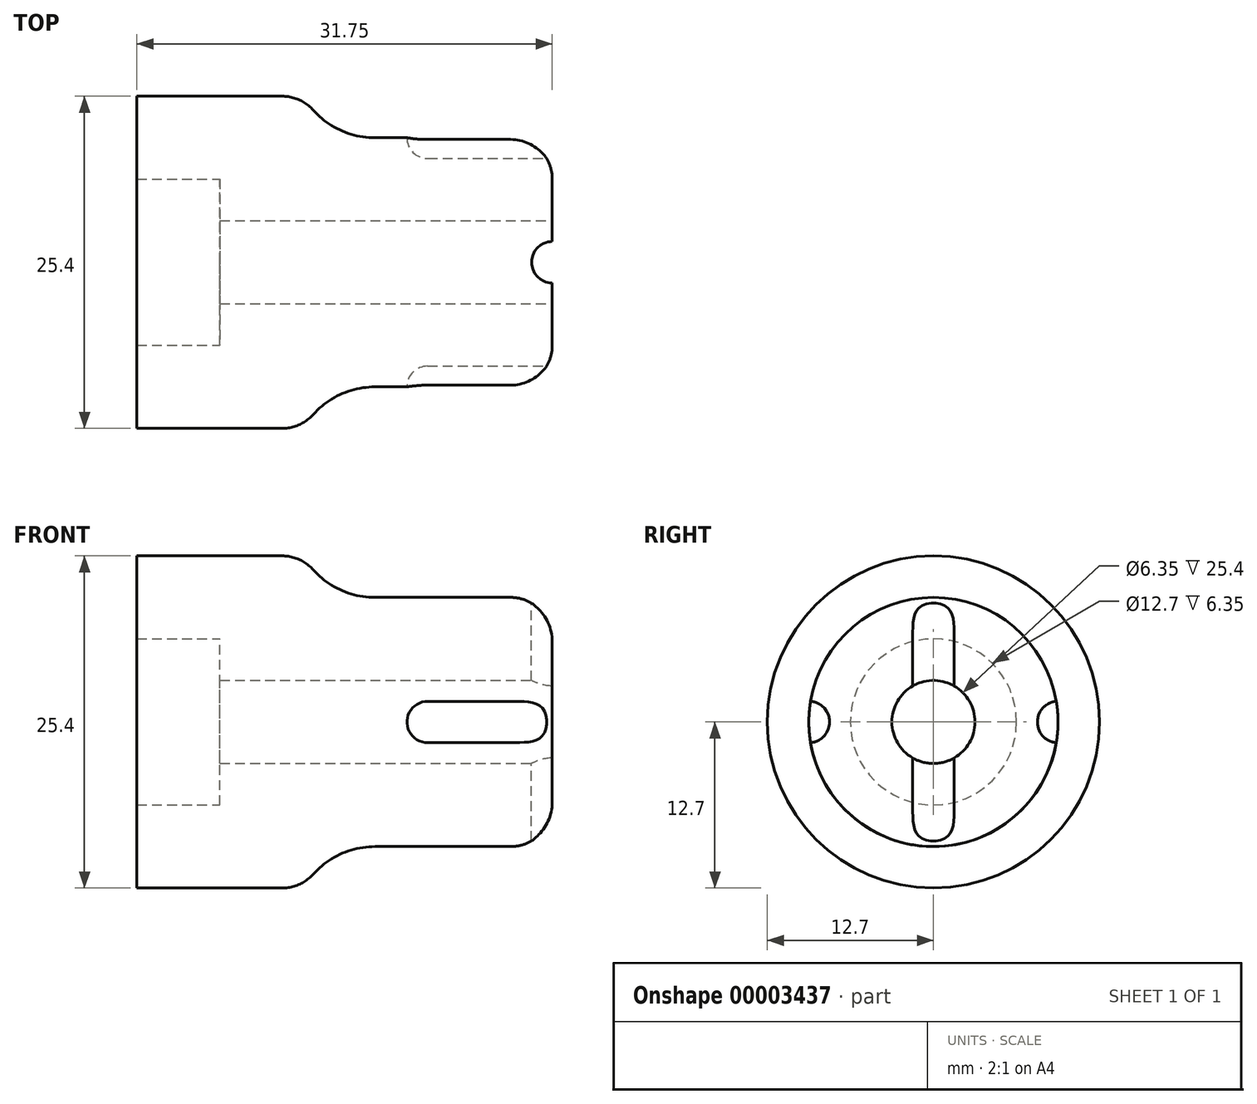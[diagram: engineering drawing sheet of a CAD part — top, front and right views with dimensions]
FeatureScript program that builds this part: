
annotation { "Feature Type Name" : "Feature", "Feature Type Description" : "" }
export const myFeature = defineFeature(function(context is Context, id is Id, definition is map)
    precondition{}
    {
        {
            var Q0;
            Q0=qCreatedBy(makeId("Front.planeOp"),FACE);
            var sketch = newSketch(context, id + "F0", { "sketchPlane" : qUnion([Q0])});
            skLineSegment(sketch, "E0", {"start": v(0, 3.18) * mm, "end": v(0, 9.53) * mm});
            skLineSegment(sketch, "E1", {"start": v(0, 9.53) * mm, "end": v(-19.05, 9.53) * mm});
            skLineSegment(sketch, "E2", {"start": v(-19.05, 9.53) * mm, "end": v(-19.05, 12.7) * mm});
            skLineSegment(sketch, "E3", {"start": v(-19.05, 12.7) * mm, "end": v(-31.75, 12.7) * mm});
            skLineSegment(sketch, "E4", {"start": v(-31.75, 12.7) * mm, "end": v(-31.75, 6.35) * mm});
            skLineSegment(sketch, "E5", {"start": v(-31.75, 6.35) * mm, "end": v(-25.4, 6.35) * mm});
            skLineSegment(sketch, "E6", {"start": v(-25.4, 6.35) * mm, "end": v(-25.4, 3.18) * mm});
            skLineSegment(sketch, "E7", {"start": v(-25.4, 3.18) * mm, "end": v(0, 3.18) * mm});
            skLineSegment(sketch, "E8", {"start": v(0, 0) * mm, "end": v(-59.15, 0) * mm, "construction": true});
            skSolve(sketch);
        }
        {
            var Q0;
            Q0=makeQuery(id+"F0.imprint","IMPRINT",FACE,{"disambiguationData":[TD([[makeQuery(id+"F0.imprint","IMPRINT",EDGE,{"derivedFrom":sQuery(id+"F0.wireOp",EDGE,"E0")}),1.0]])]});
            var Q1;
            Q1=sQuery(id+"F0.wireOp",EDGE,"E8");
            revolve(context, id + "F1", {"entities" : qUnion([Q0]), "axis" : qUnion([Q1]), "revolveType" : RevolveType.FULL});
        }
        {
            var Q0;
            Q0=makeQuery(id+"F1.opRevolve","SWEPT_EDGE",EDGE,{"disambiguationData":[OSD([sQuery(id+"F0.wireOp",EDGE,"E1"),sQuery(id+"F0.wireOp",EDGE,"E2")])]});
            fillet(context, id + "F2", {"entities" : qUnion([Q0]), "radius" : 6.35 * mm, "tangentPropagation" : true, "allowEdgeOverflow" : false});
        }
        {
            var Q0;
            Q0=makeQuery(id+"F1.opRevolve","SWEPT_EDGE",EDGE,{"disambiguationData":[OSD([sQuery(id+"F0.wireOp",EDGE,"E0"),sQuery(id+"F0.wireOp",EDGE,"E1")])]});
            var Q1;
            Q1=makeQuery(id+"F2.opFillet","BLEND_EDGE",EDGE,{"blendedFrom":[makeQuery(id+"F1.opRevolve","SWEPT_EDGE",EDGE,{"disambiguationData":[OSD([sQuery(id+"F0.wireOp",EDGE,"E1"),sQuery(id+"F0.wireOp",EDGE,"E2")])]}),makeQuery(id+"F1.opRevolve","SWEPT_FACE",FACE,{"disambiguationData":[OSD([sQuery(id+"F0.wireOp",EDGE,"E3")])]})],"blendedInto":[makeQuery(id+"F1.opRevolve","SWEPT_FACE",FACE,{"disambiguationData":[OSD([sQuery(id+"F0.wireOp",EDGE,"E3")])]})]});
            fillet(context, id + "F3", {"entities" : qUnion([Q0, Q1]), "radius" : 3.17 * mm, "tangentPropagation" : true, "allowEdgeOverflow" : false});
        }
        {
            var Q0;
            Q0=qCreatedBy(makeId("Top.planeOp"),FACE);
            var sketch = newSketch(context, id + "F4", { "sketchPlane" : qUnion([Q0])});
            skCircle(sketch, "E9", {"center": v(0, 0) * mm, "radius": 1.59 * mm});
            skSolve(sketch);
        }
        {
            var Q0;
            Q0=makeQuery(id+"F4.imprint","IMPRINT",FACE,{"disambiguationData":[TD([[makeQuery(id+"F4.imprint","IMPRINT",EDGE,{"derivedFrom":sQuery(id+"F4.wireOp",EDGE,"E9")}),1.0]])]});
            extrude(context, id + "F5", {"entities" : qUnion([Q0]), "operationType" : NewBodyOperationType.REMOVE, "oppositeDirection" : true, "depth" : 25.4 * mm, "symmetric" : true});
        }
        {
            var Q0;
            Q0=makeQuery(id+"F5.boolean.opBoolean","SPLIT",FACE,{"disambiguationData":[OD(1.0)],"derivedFrom":makeQuery(id+"F1.opRevolve","SWEPT_FACE",FACE,{"disambiguationData":[OSD([sQuery(id+"F0.wireOp",EDGE,"E0")])]})});
            var sketch = newSketch(context, id + "F6", { "sketchPlane" : qUnion([Q0])});
            skCircle(sketch, "E10", {"center": v(9.53, 0) * mm, "radius": 1.59 * mm});
            skLineSegment(sketch, "E11", {"start": v(9.53, 0) * mm, "end": v(0, 0) * mm, "construction": true});
            skCircle(sketch, "E12", {"center": v(-9.53, 0) * mm, "radius": 1.59 * mm});
            skSolve(sketch);
        }
        {
            var Q0;
            {var subQ0=sQuery(id+"F0.wireOp",EDGE,"E0");var subQ1=makeQuery(id+"F5.boolean.opBoolean","SPLIT",EDGE,{"disambiguationData":[OD(1.0)],"derivedFrom":makeQuery(id+"F3.opFillet","BLEND_EDGE",EDGE,{"blendedFrom":[makeQuery(id+"F1.opRevolve","SWEPT_EDGE",EDGE,{"disambiguationData":[OSD([subQ0,sQuery(id+"F0.wireOp",EDGE,"E1")])]}),makeQuery(id+"F1.opRevolve","SWEPT_FACE",FACE,{"disambiguationData":[OSD([subQ0])]})],"blendedInto":[makeQuery(id+"F1.opRevolve","SWEPT_FACE",FACE,{"disambiguationData":[OSD([subQ0])]})]})});var subQ2=sQuery(id+"F6.wireOp",EDGE,"E10");var subQ4=makeQuery(id+"F6.imprint","INTERSECT",VERTEX,{"disambiguationData":[OD(0.0)],"derivedFrom":[subQ1,subQ2]});Q0=qUnion([makeQuery(id+"F6.imprint","IMPRINT",FACE,{"disambiguationData":[TD([[makeQuery(id+"F6.imprint","IMPRINT",EDGE,{"derivedFrom":sQuery(id+"F6.wireOp",EDGE,"E12")}),1.0]])]}),makeQuery(id+"F6.imprint","IMPRINT",FACE,{"disambiguationData":[TD([[makeQuery(id+"F6.imprint","IMPRINT",EDGE,{"disambiguationData":[TD([[subQ4,-1.0]])],"derivedFrom":subQ2}),1.0]])]}),makeQuery(id+"F6.imprint","IMPRINT",FACE,{"disambiguationData":[TD([[makeQuery(id+"F6.imprint","IMPRINT",EDGE,{"disambiguationData":[TD([[subQ4,1.0]])],"derivedFrom":subQ2}),1.0]])]})]);}
            extrude(context, id + "F7", {"entities" : qUnion([Q0]), "operationType" : NewBodyOperationType.REMOVE, "oppositeDirection" : true, "depth" : 9.52 * mm});
        }
        {
            var Q0;
            Q0=makeQuery(id+"F7.boolean.opBoolean","COPY",FACE,{"derivedFrom":makeQuery(id+"F7.opExtrude","CAP_FACE",FACE,{"disambiguationData":[OSD([sQuery(id+"F6.wireOp",EDGE,"E12")])],"isStart":false})});
            var sketch = newSketch(context, id + "F8", { "sketchPlane" : qUnion([Q0])});
            skLineSegment(sketch, "E13", {"start": v(-9.53, 1.59) * mm, "end": v(-9.53, -1.59) * mm});
            skArc(sketch, "E14.converted", {"start": v(-9.53, -1.59) * mm, "mid": v(-7.94, 0) * mm, "end": v(-9.53, 1.59) * mm});
            skPoint(sketch, "E15.orphan", {"position": v(-9.4, 1.58) * mm});
            skSolve(sketch);
        }
        {
            var Q0;
            {var subQ0=makeQuery(id+"F7.boolean.opBoolean","INTERSECT",EDGE,{"derivedFrom":[makeQuery(id+"F1.opRevolve","SWEPT_FACE",FACE,{"disambiguationData":[OSD([sQuery(id+"F0.wireOp",EDGE,"E1")])]}),makeQuery(id+"F7.opExtrude","CAP_FACE",FACE,{"disambiguationData":[OSD([sQuery(id+"F6.wireOp",EDGE,"E12")])],"isStart":false})]});var subQ1=sQuery(id+"F8.wireOp",EDGE,"E13");var subQ3=sQuery(id+"F8.wireOp",EDGE,"E14.converted");var subQ6=makeQuery(id+"F8.imprint","INTERSECT",VERTEX,{"disambiguationData":[OD(0.0)],"derivedFrom":[subQ1,subQ3]});var subQ7=makeQuery(id+"F8.imprint","INTERSECT",VERTEX,{"disambiguationData":[OD(0.0)],"derivedFrom":[subQ0,subQ3]});var subQ9=makeQuery(id+"F8.imprint","INTERSECT",VERTEX,{"disambiguationData":[OD(1.0)],"derivedFrom":[subQ1,subQ3]});Q0=qUnion([makeQuery(id+"F8.imprint","IMPRINT",FACE,{"disambiguationData":[TD([[makeQuery(id+"F8.imprint","IMPRINT",EDGE,{"disambiguationData":[TD([[subQ6,-1.0]])],"derivedFrom":subQ1}),1.0]])]}),makeQuery(id+"F8.imprint","IMPRINT",FACE,{"disambiguationData":[TD([[makeQuery(id+"F8.imprint","IMPRINT",EDGE,{"disambiguationData":[TD([[subQ9,1.0]])],"derivedFrom":subQ1}),1.0]])]}),makeQuery(id+"F8.imprint","IMPRINT",FACE,{"disambiguationData":[TD([[makeQuery(id+"F8.imprint","IMPRINT",EDGE,{"disambiguationData":[TD([[subQ7,-1.0]])],"derivedFrom":subQ3}),1.0]])]})]);}
            var Q1;
            Q1=sQuery(id+"F8.wireOp",EDGE,"E13");
            revolve(context, id + "F9", {"operationType" : NewBodyOperationType.REMOVE, "entities" : qUnion([Q0]), "axis" : qUnion([Q1]), "revolveType" : RevolveType.FULL, "oppositeDirection" : true});
        }
        {
            var Q0;
            Q0=makeQuery(id+"F7.boolean.opBoolean","COPY",FACE,{"derivedFrom":makeQuery(id+"F7.opExtrude","CAP_FACE",FACE,{"disambiguationData":[OSD([sQuery(id+"F6.wireOp",EDGE,"E10")])],"isStart":false})});
            var sketch = newSketch(context, id + "F10", { "sketchPlane" : qUnion([Q0])});
            skLineSegment(sketch, "E16", {"start": v(9.53, 1.59) * mm, "end": v(9.53, -1.59) * mm});
            skArc(sketch, "E17.converted", {"start": v(9.53, 1.59) * mm, "mid": v(7.94, 0) * mm, "end": v(9.53, -1.59) * mm});
            skPoint(sketch, "E18.orphan", {"position": v(9.4, 1.58) * mm});
            skSolve(sketch);
        }
        {
            var Q0;
            {var subQ0=makeQuery(id+"F7.boolean.opBoolean","INTERSECT",EDGE,{"derivedFrom":[makeQuery(id+"F1.opRevolve","SWEPT_FACE",FACE,{"disambiguationData":[OSD([sQuery(id+"F0.wireOp",EDGE,"E1")])]}),makeQuery(id+"F7.opExtrude","CAP_FACE",FACE,{"disambiguationData":[OSD([sQuery(id+"F6.wireOp",EDGE,"E10")])],"isStart":false})]});var subQ1=sQuery(id+"F10.wireOp",EDGE,"E16");var subQ3=sQuery(id+"F10.wireOp",EDGE,"E17.converted");var subQ6=makeQuery(id+"F10.imprint","INTERSECT",VERTEX,{"disambiguationData":[OD(0.0)],"derivedFrom":[subQ1,subQ3]});var subQ7=makeQuery(id+"F10.imprint","INTERSECT",VERTEX,{"disambiguationData":[OD(0.0)],"derivedFrom":[subQ0,subQ3]});var subQ9=makeQuery(id+"F10.imprint","INTERSECT",VERTEX,{"disambiguationData":[OD(1.0)],"derivedFrom":[subQ1,subQ3]});Q0=qUnion([makeQuery(id+"F10.imprint","IMPRINT",FACE,{"disambiguationData":[TD([[makeQuery(id+"F10.imprint","IMPRINT",EDGE,{"disambiguationData":[TD([[subQ6,-1.0]])],"derivedFrom":subQ1}),-1.0]])]}),makeQuery(id+"F10.imprint","IMPRINT",FACE,{"disambiguationData":[TD([[makeQuery(id+"F10.imprint","IMPRINT",EDGE,{"disambiguationData":[TD([[subQ9,1.0]])],"derivedFrom":subQ1}),-1.0]])]}),makeQuery(id+"F10.imprint","IMPRINT",FACE,{"disambiguationData":[TD([[makeQuery(id+"F10.imprint","IMPRINT",EDGE,{"disambiguationData":[TD([[subQ7,1.0]])],"derivedFrom":subQ3}),1.0]])]})]);}
            var Q1;
            Q1=sQuery(id+"F10.wireOp",EDGE,"E16");
            revolve(context, id + "F11", {"operationType" : NewBodyOperationType.REMOVE, "entities" : qUnion([Q0]), "axis" : qUnion([Q1]), "revolveType" : RevolveType.FULL, "oppositeDirection" : true});
        }
    });
